# Revit family: Table-Teknion-CWTK_C-D_Rectangular_Table_Knife_Edge-R2022
name_source: partatom
category: Furniture
units: mm (PartAtom-declared; Revit-internal decimal feet)

## family parameters
Always vertical = Yes
Cut with Voids When Loaded = No
OmniClass Number = 23.40.20.00
OmniClass Title = General Furniture and Specialties
Render Appearance Source = Family Geometry
Room Calculation Point = No
Shared = Yes
Work Plane-Based = No

## types (2) — shared parameters
Assembly Code = E2020200
Description = Custom Wood C+D Rectangular Table, Knife Edge
For Additional Finishes, please visit = https://assets.teknion.com
Manufacturer = Teknion
Manufacturer Fax = 416.661.4586
Model = CWTK__
Part Number = CWTK
Product Documentation Link = https://assets.teknion.com
Product Line = C+D
Product Page URL = https://www.teknion.com
Series = Custom Wood
Sustainability Data = https://www.teknion.com
To render, please download texture images found here = https://assets.teknion.com
URL = www.teknion.com
Unit Weight URL = http://www.teknion.com
Warranty = http://www.teknion.com
zero-valued in all types: Default Elevation

## type names
- Round Corner Style
- Square Corner Style
type visibility flags: 2 boolean params named "<type name> Worksurface" — each type sets only its own to Yes (folded from table)

## geometry (parser evidence)
native form markers: Sweep x13
no freeform markers — native parametric forms only
